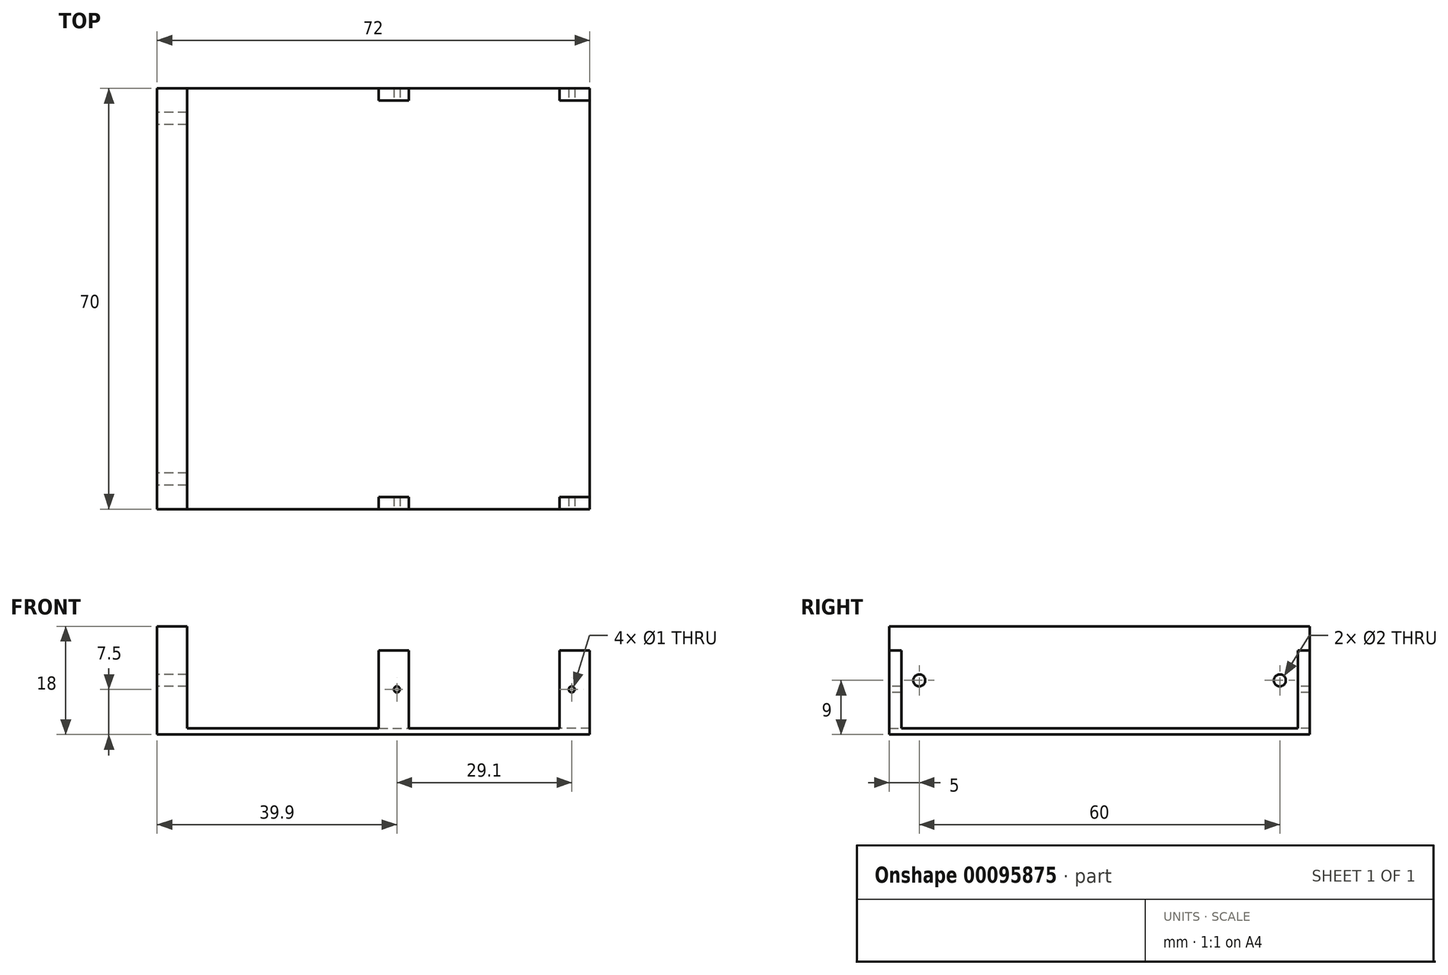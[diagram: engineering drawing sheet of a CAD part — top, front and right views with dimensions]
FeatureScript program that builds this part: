
annotation { "Feature Type Name" : "Feature", "Feature Type Description" : "" }
export const myFeature = defineFeature(function(context is Context, id is Id, definition is map)
    precondition{}
    {
        {
            var Q0;
            Q0=qCreatedBy(makeId("Top.planeOp"),FACE);
            var sketch = newSketch(context, id + "F0", { "sketchPlane" : qUnion([Q0])});
            skLineSegment(sketch, "E0.bottom", {"start": v(-40, 20) * mm, "end": v(32, 20) * mm});
            skLineSegment(sketch, "E0.top", {"start": v(-40, -50) * mm, "end": v(32, -50) * mm});
            skLineSegment(sketch, "E0.left", {"start": v(-40, 20) * mm, "end": v(-40, -50) * mm});
            skLineSegment(sketch, "E0.right", {"start": v(32, 20) * mm, "end": v(32, -50) * mm});
            skSolve(sketch);
        }
        {
            var Q0;
            Q0 = qSketchRegion(id + "F0", true);
            extrude(context, id + "F1", {"entities" : qUnion([Q0]), "depth" : 1 * mm});
        }
        {
            var Q0;
            Q0=makeQuery(id+"F1.opExtrude","CAP_FACE",FACE,{"disambiguationData":[OSD([sQuery(id+"F0.wireOp",EDGE,"E0.bottom"),sQuery(id+"F0.wireOp",EDGE,"E0.top"),sQuery(id+"F0.wireOp",EDGE,"E0.left"),sQuery(id+"F0.wireOp",EDGE,"E0.right")])],"isStart":false});
            var sketch = newSketch(context, id + "F2", { "sketchPlane" : qUnion([Q0])});
            skLineSegment(sketch, "E1.bottom", {"start": v(-40, 20) * mm, "end": v(-35, 20) * mm});
            skLineSegment(sketch, "E1.top", {"start": v(-40, -50) * mm, "end": v(-35, -50) * mm});
            skLineSegment(sketch, "E1.left", {"start": v(-40, 20) * mm, "end": v(-40, -50) * mm});
            skLineSegment(sketch, "E1.right", {"start": v(-35, 20) * mm, "end": v(-35, -50) * mm});
            skLineSegment(sketch, "E2.bottom", {"start": v(32, 20) * mm, "end": v(27, 20) * mm});
            skLineSegment(sketch, "E2.top", {"start": v(32, 18) * mm, "end": v(27, 18) * mm});
            skLineSegment(sketch, "E2.left", {"start": v(32, 20) * mm, "end": v(32, 18) * mm});
            skLineSegment(sketch, "E2.right", {"start": v(27, 20) * mm, "end": v(27, 18) * mm});
            skLineSegment(sketch, "E3.bottom", {"start": v(-3.1, 20) * mm, "end": v(1.9, 20) * mm});
            skLineSegment(sketch, "E3.top", {"start": v(-3.1, 18) * mm, "end": v(1.9, 18) * mm});
            skLineSegment(sketch, "E3.left", {"start": v(-3.1, 20) * mm, "end": v(-3.1, 18) * mm});
            skLineSegment(sketch, "E3.right", {"start": v(1.9, 20) * mm, "end": v(1.9, 18) * mm});
            skLineSegment(sketch, "E4.bottom", {"start": v(32, -50) * mm, "end": v(27, -50) * mm});
            skLineSegment(sketch, "E4.top", {"start": v(32, -48) * mm, "end": v(27, -48) * mm});
            skLineSegment(sketch, "E4.left", {"start": v(32, -50) * mm, "end": v(32, -48) * mm});
            skLineSegment(sketch, "E4.right", {"start": v(27, -50) * mm, "end": v(27, -48) * mm});
            skLineSegment(sketch, "E5.bottom", {"start": v(-3.1, -50) * mm, "end": v(1.9, -50) * mm});
            skLineSegment(sketch, "E5.top", {"start": v(-3.1, -48) * mm, "end": v(1.9, -48) * mm});
            skLineSegment(sketch, "E5.left", {"start": v(-3.1, -50) * mm, "end": v(-3.1, -48) * mm});
            skLineSegment(sketch, "E5.right", {"start": v(1.9, -50) * mm, "end": v(1.9, -48) * mm});
            skSolve(sketch);
        }
        {
            var Q0;
            Q0=makeQuery(id+"F2.imprint","IMPRINT",FACE,{"disambiguationData":[TD([[makeQuery(id+"F2.imprint","IMPRINT",EDGE,{"derivedFrom":sQuery(id+"F2.wireOp",EDGE,"E1.bottom")}),-1.0]])]});
            extrude(context, id + "F3", {"entities" : qUnion([Q0]), "operationType" : NewBodyOperationType.ADD, "depth" : 17 * mm});
        }
        {
            var Q0;
            Q0=makeQuery(id+"F3.boolean.opBoolean","MERGE",FACE,{"derivedFrom":[makeQuery(id+"F1.opExtrude","SWEPT_FACE",FACE,{"disambiguationData":[OSD([sQuery(id+"F0.wireOp",EDGE,"E0.left")])]}),makeQuery(id+"F3.opExtrude","SWEPT_FACE",FACE,{"disambiguationData":[OSD([sQuery(id+"F2.wireOp",EDGE,"E1.left")])]})]});
            var sketch = newSketch(context, id + "F4", { "sketchPlane" : qUnion([Q0])});
            skCircle(sketch, "E6", {"center": v(-15, 9) * mm, "radius": 1 * mm});
            skPoint(sketch, "E6.centerSnap0", {"position": v(-20, 9) * mm});
            skCircle(sketch, "E7", {"center": v(45, 9) * mm, "radius": 1 * mm});
            skSolve(sketch);
        }
        {
            var Q0;
            Q0 = qSketchRegion(id + "F4", true);
            var Q1;
            Q1=makeQuery(id+"F3.opExtrude","SWEPT_FACE",FACE,{"disambiguationData":[OSD([sQuery(id+"F2.wireOp",EDGE,"E1.right")])]});
            extrude(context, id + "F5", {"entities" : qUnion([Q0]), "operationType" : NewBodyOperationType.REMOVE, "endBound" : BoundingType.UP_TO_SURFACE, "oppositeDirection" : true, "endBoundEntityFace" : qUnion([Q1]), "depth" : 25 * mm});
        }
        {
            var Q0;
            Q0=makeQuery(id+"F2.imprint","IMPRINT",FACE,{"disambiguationData":[TD([[makeQuery(id+"F2.imprint","IMPRINT",EDGE,{"derivedFrom":sQuery(id+"F2.wireOp",EDGE,"E3.bottom")}),-1.0]])]});
            var Q1;
            Q1=makeQuery(id+"F2.imprint","IMPRINT",FACE,{"disambiguationData":[TD([[makeQuery(id+"F2.imprint","IMPRINT",EDGE,{"derivedFrom":sQuery(id+"F2.wireOp",EDGE,"E2.bottom")}),-1.0]])]});
            var Q2;
            Q2=makeQuery(id+"F2.imprint","IMPRINT",FACE,{"disambiguationData":[TD([[makeQuery(id+"F2.imprint","IMPRINT",EDGE,{"derivedFrom":sQuery(id+"F2.wireOp",EDGE,"E5.bottom")}),1.0]])]});
            var Q3;
            Q3=makeQuery(id+"F2.imprint","IMPRINT",FACE,{"disambiguationData":[TD([[makeQuery(id+"F2.imprint","IMPRINT",EDGE,{"derivedFrom":sQuery(id+"F2.wireOp",EDGE,"E4.bottom")}),1.0]])]});
            extrude(context, id + "F6", {"entities" : qUnion([Q0, Q1, Q2, Q3]), "operationType" : NewBodyOperationType.ADD, "depth" : 13 * mm});
        }
        {
            var Q0;
            Q0=makeQuery(id+"F6.boolean.opBoolean","MERGE",FACE,{"derivedFrom":[makeQuery(id+"F3.boolean.opBoolean","MERGE",FACE,{"derivedFrom":[makeQuery(id+"F1.opExtrude","SWEPT_FACE",FACE,{"disambiguationData":[OSD([sQuery(id+"F0.wireOp",EDGE,"E0.top")])]}),makeQuery(id+"F3.opExtrude","SWEPT_FACE",FACE,{"disambiguationData":[OSD([sQuery(id+"F2.wireOp",EDGE,"E1.top")])]})]}),makeQuery(id+"F6.opExtrude","SWEPT_FACE",FACE,{"disambiguationData":[OSD([sQuery(id+"F2.wireOp",EDGE,"E4.bottom")])]}),makeQuery(id+"F6.opExtrude","SWEPT_FACE",FACE,{"disambiguationData":[OSD([sQuery(id+"F2.wireOp",EDGE,"E5.bottom")])]})]});
            var sketch = newSketch(context, id + "F7", { "sketchPlane" : qUnion([Q0])});
            skCircle(sketch, "E8", {"center": v(-0.1, 7.5) * mm, "radius": 0.5 * mm});
            skCircle(sketch, "E9", {"center": v(29, 7.5) * mm, "radius": 0.5 * mm});
            skSolve(sketch);
        }
        {
            var Q0;
            Q0 = qSketchRegion(id + "F7", true);
            extrude(context, id + "F8", {"entities" : qUnion([Q0]), "operationType" : NewBodyOperationType.REMOVE, "endBound" : BoundingType.THROUGH_ALL, "oppositeDirection" : true, "depth" : 25 * mm});
        }
    });
